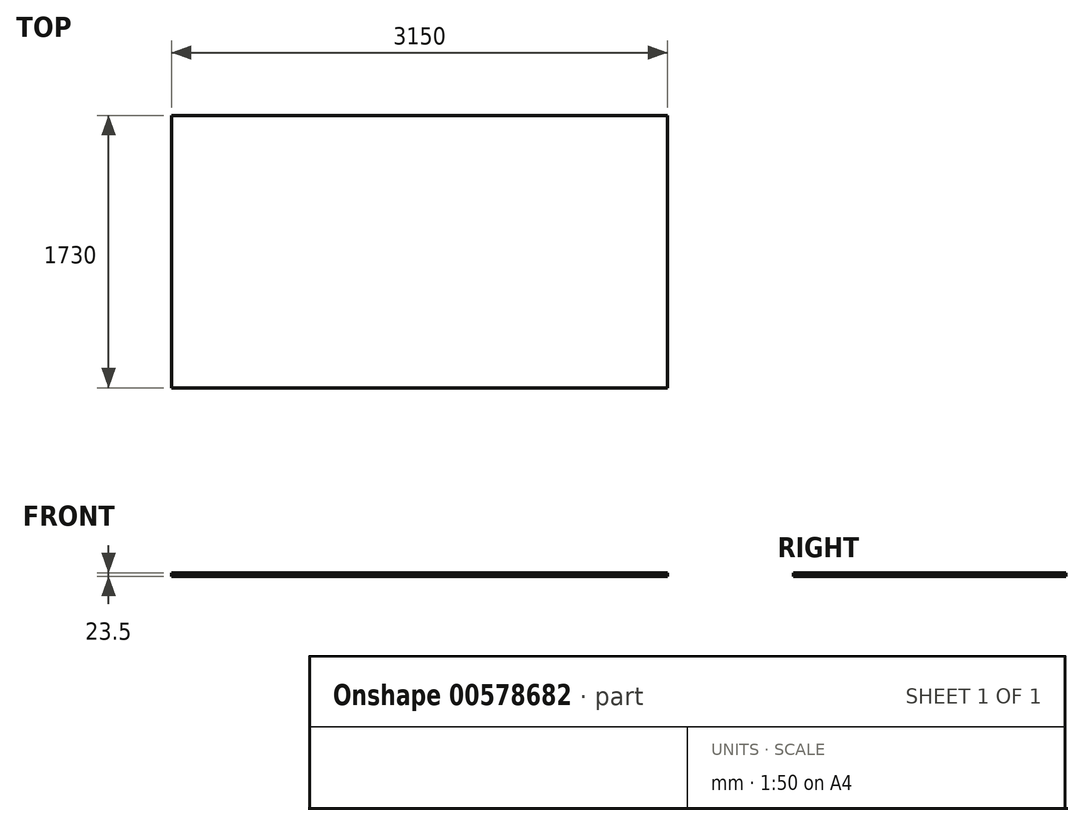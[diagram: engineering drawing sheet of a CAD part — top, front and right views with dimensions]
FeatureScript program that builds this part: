
annotation { "Feature Type Name" : "Feature", "Feature Type Description" : "" }
export const myFeature = defineFeature(function(context is Context, id is Id, definition is map)
    precondition{}
    {
        {
            var Q0;
            Q0=qCreatedBy(makeId("Top.planeOp"),FACE);
            var sketch = newSketch(context, id + "F0", { "sketchPlane" : qUnion([Q0])});
            skLineSegment(sketch, "E0.bottom", {"start": v(1553.3, 877.79) * mm, "end": v(-1596.7, 877.79) * mm});
            skLineSegment(sketch, "E0.top", {"start": v(1553.3, -852.21) * mm, "end": v(-1596.7, -852.21) * mm});
            skLineSegment(sketch, "E0.left", {"start": v(1553.3, 877.79) * mm, "end": v(1553.3, -852.21) * mm});
            skLineSegment(sketch, "E0.right", {"start": v(-1596.7, 877.79) * mm, "end": v(-1596.7, -852.21) * mm});
            skPoint(sketch, "E0.middle", {"position": v(-21.7, 12.79) * mm});
            skSolve(sketch);
        }
        {
            var Q0;
            Q0=makeQuery(id+"F0.imprint","IMPRINT",FACE,{"disambiguationData":[TD([[makeQuery(id+"F0.imprint","IMPRINT",EDGE,{"derivedFrom":sQuery(id+"F0.wireOp",EDGE,"E0.bottom")}),1.0]])]});
            extrude(context, id + "F1", {"entities" : qUnion([Q0]), "depth" : 23.5 * mm, "offsetDistance" : 25 * mm});
        }
    });
